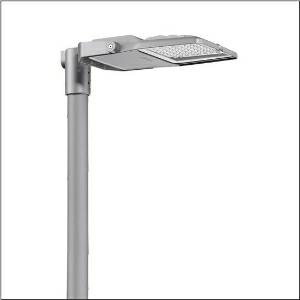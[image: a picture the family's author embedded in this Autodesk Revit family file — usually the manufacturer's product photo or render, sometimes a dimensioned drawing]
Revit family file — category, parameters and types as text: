
# Revit family: floodlight_fl_21_iq_mini___pl33t_5xa7772c4f3a_1e48
name_source: partatom
category: Lighting Fixtures
units: mm (PartAtom-declared; Revit-internal decimal feet)

## family parameters
Cut with Voids When Loaded = No
Host = Face
Light Source = No
Part Type = Normal
Room Calculation Point = No
Round Connector Dimension = Use Diameter
Shared = No

## types (1)
- --- (1 x LED, 12570 lm, 87.2 W, 4000K)
    Apparent Load = 87 VA
    CIE Flux Codes = 26 75 99 100 100
    Color Rendering = 70
    Color Temperature = 4000K
    Default Elevation = 1800 mm
    Description = Floodlight FL 21 iQ mini, floodlight, primary light control with lens, of PMMA, primary optical cover: protective disc, of toughened safety glass, transparent, light distribution: PL33T, light emission: direct distribution, installation type: surface-mounted, LED, High Power LED, rated luminous flux: 12.570lm, luminous efficacy: 144lm/W, light colour: 740, colour temperature: 4000K, control gear: iQ Street-Remote/DALI, control: Auto-Match, Temp-Guard, Night-Set, Smart-Wire, Desk-Remote (wireless, voltage-free reading and setting of iQ features in the workshop via application-optimized NFC function/RFID function), optimised constant luminous flux control (CLO 2.0), Light-Fading, Lumen-Switch, with terminal, 6-pole, mains connection: 220..240V, AC, 50/60Hz, start of lifetime: 87W, end of service life: 92W, reduction: 40W, luminaire housing, of diecast aluminium, powder-coated, Siteco® metallic grey (DB 702S), corrosivity category C5 mid according to DIN EN ISO 12944, suitable for swimming pools, chlorine-resistant, sealing non-destructively replaceable, please order mast flange separately, mast bracket, of steel, galvanised, powder-coated, protection rating (complete): IP66, insulation class (complete): insulation class II (safety insulation), certification: CE, ENEC, VDE, protection symbol: D, impact resistance: IK08, permissible operating ambient temperature: -40..+40°C, permissible operating ambient temperature for outdoor applications: -40..+50°C, standard: DIN EN 12944, LABS conformity tested according to VDMA 24364:2018-05, packaging unit: 1 piece

Light Distribution: PL33T
    Height = 70 mm
    Lamp = 1 x LED
    Lamp Light Flux = 12570 lm
    Lamp Power = 87.2 W
    Lamp count = 1
    Length = 485 mm
    Luminous efficacy = 144 lm/W
    Manufacturer = Siteco
    ModVariant = No
    Model = 5XA7772C4F3A
    Number of Poles = 1
    OnlyDefault = Yes
    Power Factor = 1
    Product Name = Floodlight FL 21 iQ mini | PL33T
    Product group = floodlight | pylon annexe
    ProductGroupID = 6200
    Protection Class = Protection class II
    Protection Degree = IP 66
    RLX_Detail_Level = 1
    RLX_Emergency_Light_Flux = 0 lm
    RLX_Emergency_Type = 0
    RLX_Emergency_Type_DB = No
    RlxData = <blob elided: 101277 chars, md5=6d5a96b6>
    Socket = socket
    Standby Power = 0 W
    System Light Flux = 12570 lm
    System Power = 87 W
    Type Comments = factory setting: luminous flux: 100 % | dim-lin: 254 | 456 mA
    Type Image = l_1007125.jpg
    URL = http://relux.com
    VarID = @adj_149348
    Voltage = 0 V
    Weight = 0.00 kg
    Width = 337 mm

## geometry (parser evidence)
native form markers: Blend x4, Sweep x13
no freeform markers — native parametric forms only
